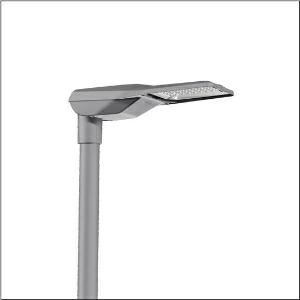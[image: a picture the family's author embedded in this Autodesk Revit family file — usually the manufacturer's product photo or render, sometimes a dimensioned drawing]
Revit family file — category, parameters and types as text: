
# Revit family: streetlight_sl_21_mini___st1_0a_5xe6d63a08hb_d3ee
name_source: partatom
category: Lighting Fixtures
units: mm (PartAtom-declared; Revit-internal decimal feet)

## family parameters
Cut with Voids When Loaded = No
Host = Face
Light Source = No
Part Type = Normal
Room Calculation Point = No
Round Connector Dimension = Use Diameter
Shared = No

## types (1)
- --- (1 x LED, 8110 lm, 66 W, 2700K)
    Apparent Load = 66 VA
    CIE Flux Codes = 37 72 97 100 100
    Color Rendering = 70
    Color Temperature = 2700K
    Default Elevation = 1800 mm
    Description = Streetlight SL 21 mini, mast luminaire, primary light control with lens, of PMMA, primary optical cover: cover, of toughened safety glass, transparent, light distribution: ST1.0a, light emission: direct distribution, primary light characteristic: asymmetric, installation type: post-top, side-entry, LED, 3G 1.5mm², High Power LED, rated luminous flux: 8.110lm, luminous efficacy: 123lm/W, light colour: 727, colour temperature: 2700K, control: overheat protection, constant luminous flux control, time-dependent luminous flux control, flexible luminous flux parameterisation, mains connection: 230..240V, AC, 50/60Hz, connection cable pre-assembled, cable length: 8,5m, wiring characteristics: H07RN-F, start of lifetime: 66W, end of service life: 69W, reduction: 30W, luminaire housing, of diecast aluminium, powder-coated, Siteco® metallic grey (DB 702S), corrosivity category C5 mid according to DIN EN ISO 12944, please order mast flange separately, inclination adjustable: 0°, 5°, 10°, 15°, sealing non-destructively replaceable, multi-level sealing system, length: 628mm, width: 235mm, height: 110mm, mast flange for spigot size: 42mm (side-entry): 5XC10008XM4, 60/48mm (side-entry/post-top): 5XC10108XM2, 76/60mm (side-entry/post-top): 5XC10108XM1, protection rating (complete): IP66, insulation class (complete): insulation class II (safety insulation), certification: CE, ENEC, ENEC+, VDE, impact resistance: IK09, permissible operating ambient temperature for outdoor applications: -40..+50°C, standard-compliant lighting for roads and squares, packaging unit: 1 piece

Light Distribution: ST1.0a
    Height = 110 mm
    Lamp = 1 x LED
    Lamp Light Flux = 8110 lm
    Lamp Power = 66 W
    Lamp count = 1
    Length = 625 mm
    Luminous efficacy = 123 lm/W
    Manufacturer = Siteco
    ModVariant = No
    Model = 5XE6D63A08HB
    Number of Poles = 1
    OnlyDefault = Yes
    Power Factor = 1
    Product Name = Streetlight SL 21 mini | ST1.0a
    Product group = mast luminaire | pylon top
    ProductGroupID = 6100
    Protection Class = Protection class II
    Protection Degree = IP 66
    RLX_Detail_Level = 1
    RLX_Emergency_Light_Flux = 0 lm
    RLX_Emergency_Type = 0
    RLX_Emergency_Type_DB = No
    RlxData = <blob elided: 92165 chars, md5=83348a58>
    Socket = socket
    Standby Power = 0 W
    System Light Flux = 8110 lm
    System Power = 66 W
    Type Comments = factory setting: luminous flux: 100 % | Output Level: 100 % | 670 mA
    Type Image = l_1003519.jpg
    URL = http://relux.com
    VarID = @adj_140233
    Voltage = 0 V
    Weight = 0.00 kg
    Width = 234 mm

## geometry (parser evidence)
native form markers: Blend x4, Sweep x12
no freeform markers — native parametric forms only
